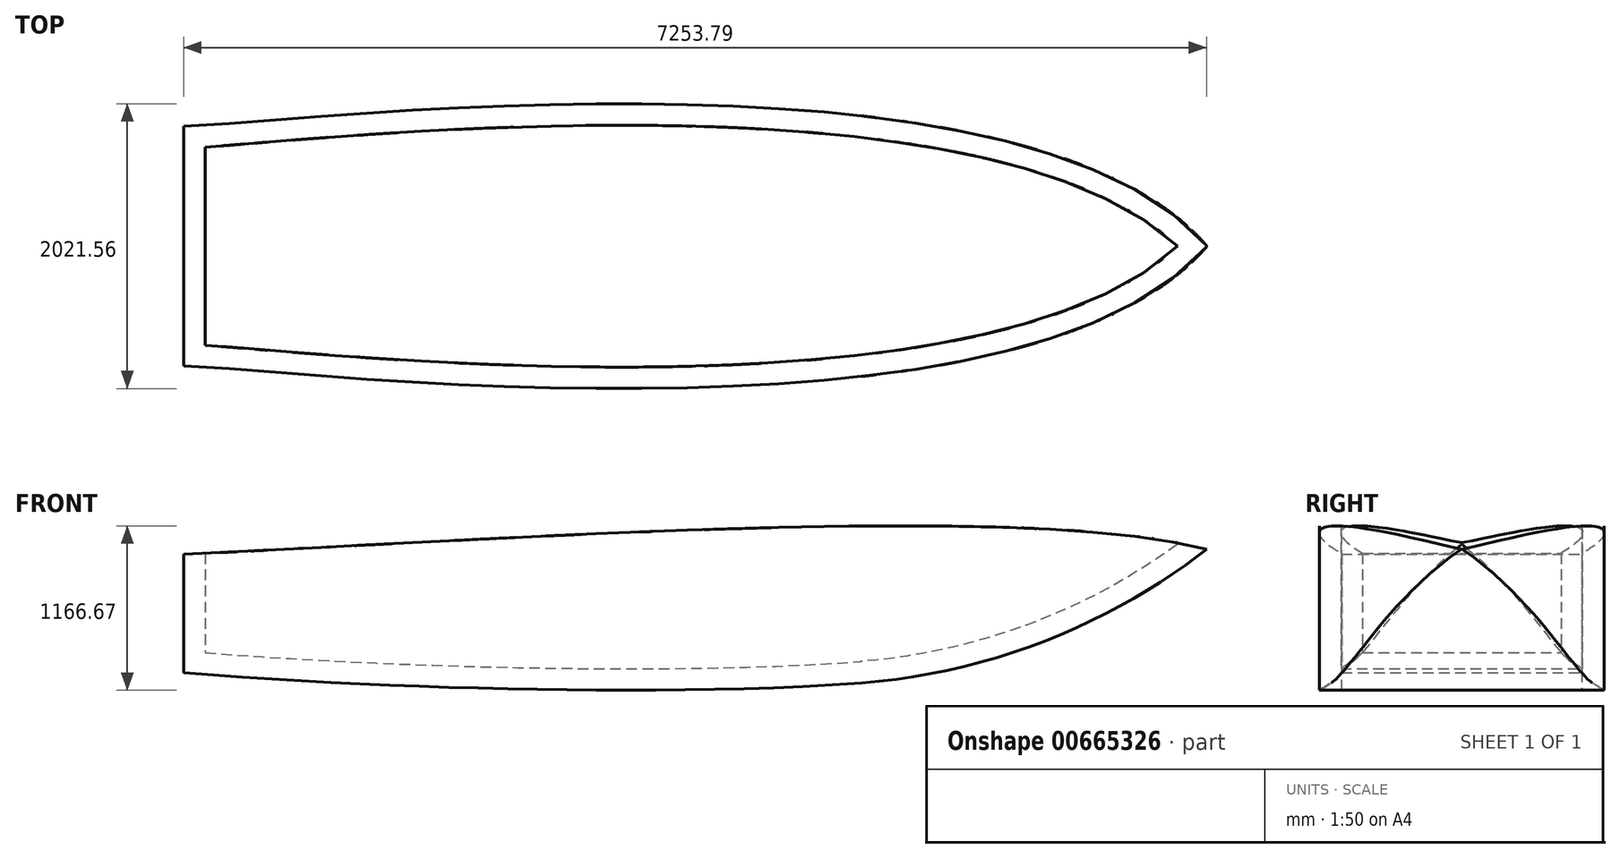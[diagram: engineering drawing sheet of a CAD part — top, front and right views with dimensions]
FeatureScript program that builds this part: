
annotation { "Feature Type Name" : "Feature", "Feature Type Description" : "" }
export const myFeature = defineFeature(function(context is Context, id is Id, definition is map)
    precondition{}
    {
        {
            var Q0;
            Q0=qCreatedBy(makeId("Front.planeOp"),FACE);
            var sketch = newSketch(context, id + "F0", { "sketchPlane" : qUnion([Q0])});
            skFitSpline(sketch, "E0", {"points": [v(2286.14, 213.69) * mm, v(-3265.45, 173.92) * mm], "startDerivative": vector(-1822.5, -641.06) * mm, "endDerivative": vector(-6240.83, 521.77) * mm});
            skArc(sketch, "E1.filletArc", {"start": v(1546.6, 99.73) * mm, "mid": v(2838.74, 394.8) * mm, "end": v(3991.95, 1048.1) * mm});
            skLineSegment(sketch, "E2", {"start": v(-3265.45, 173.92) * mm, "end": v(-3275.83, 1012.12) * mm});
            skFitSpline(sketch, "E3", {"points": [v(-3275.83, 1012.12) * mm, v(3991.95, 1048.1) * mm], "startDerivative": vector(7179.52, 340.71) * mm, "endDerivative": vector(3700.93, -1010.33) * mm});
            skSolve(sketch);
        }
        {
            var Q0;
            Q0 = qSketchRegion(id + "F0", true);
            extrude(context, id + "F1", {"entities" : qUnion([Q0]), "endBound" : BoundingType.SYMMETRIC, "depth" : 2032 * mm, "offsetDistance" : 25.4 * mm});
        }
        {
            var Q0;
            Q0=qCreatedBy(makeId("Top.planeOp"),FACE);
            var sketch = newSketch(context, id + "F2", { "sketchPlane" : qUnion([Q0])});
            skFitSpline(sketch, "E4", {"points": [v(-3261.84, -851.35) * mm, v(3995.55, 0) * mm], "startDerivative": vector(1071.73, 76.55) * mm, "endDerivative": vector(4050.3, 4753.19) * mm});
            skFitSpline(sketch, "E5.MirrorCS", {"points": [v(-3261.84, 851.35) * mm, v(3995.55, 0) * mm], "startDerivative": vector(1071.73, -76.55) * mm, "endDerivative": vector(4050.3, -4753.19) * mm});
            skLineSegment(sketch, "E6", {"start": v(-3261.84, 851.35) * mm, "end": v(-3261.84, -851.35) * mm});
            skSolve(sketch);
        }
        {
            var Q0;
            Q0 = qSketchRegion(id + "F2", true);
            extrude(context, id + "F3", {"entities" : qUnion([Q0]), "operationType" : NewBodyOperationType.INTERSECT, "depth" : 1905 * mm, "offsetDistance" : 25.4 * mm});
        }
        {
            var Q0;
            Q0=makeQuery(id+"F1.opExtrude","SWEPT_FACE",FACE,{"disambiguationData":[OSD([sQuery(id+"F0.wireOp",EDGE,"E3")])]});
            shell(context, id + "F4", {"entities" : qUnion([Q0]), "thickness" : 152.4 * mm});
        }
    });
